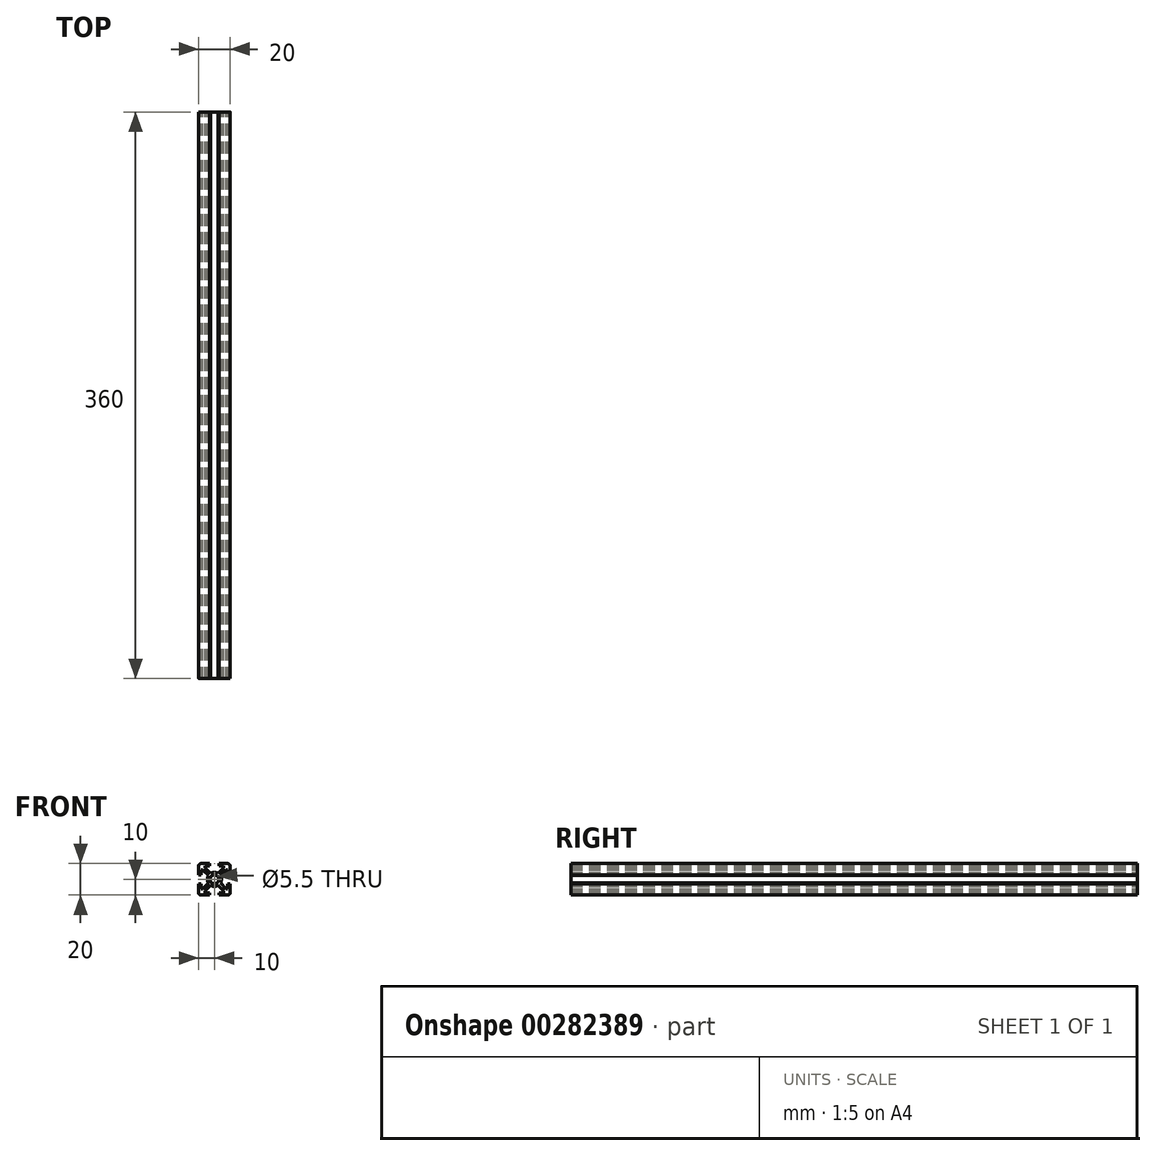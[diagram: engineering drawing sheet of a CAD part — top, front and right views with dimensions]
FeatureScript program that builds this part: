
annotation { "Feature Type Name" : "Feature", "Feature Type Description" : "" }
export const myFeature = defineFeature(function(context is Context, id is Id, definition is map)
    precondition{}
    {
        {
            var Q0;
            Q0=qCreatedBy(makeId("Front.planeOp"),FACE);
            var sketch = newSketch(context, id + "F0", { "sketchPlane" : qUnion([Q0])});
            skLineSegment(sketch, "E0.bottom", {"start": v(1.5, 0) * mm, "end": v(7, 0) * mm});
            skLineSegment(sketch, "E0.top", {"start": v(1.5, 20) * mm, "end": v(7, 20) * mm});
            skLineSegment(sketch, "E0.left", {"start": v(0, 1.5) * mm, "end": v(0, 7) * mm});
            skLineSegment(sketch, "E0.right", {"start": v(20, 1.5) * mm, "end": v(20, 7) * mm});
            skPoint(sketch, "E1.visualSharp", {"position": v(0, 20) * mm});
            skArc(sketch, "E1.filletArc", {"start": v(1.5, 20) * mm, "mid": v(0.44, 19.56) * mm, "end": v(0, 18.5) * mm});
            skPoint(sketch, "E2.visualSharp", {"position": v(20, 20) * mm});
            skArc(sketch, "E2.filletArc", {"start": v(20, 18.5) * mm, "mid": v(19.56, 19.56) * mm, "end": v(18.5, 20) * mm});
            skPoint(sketch, "E3.visualSharp", {"position": v(20, 0) * mm});
            skArc(sketch, "E3.filletArc", {"start": v(18.5, 0) * mm, "mid": v(19.56, 0.44) * mm, "end": v(20, 1.5) * mm});
            skPoint(sketch, "E4.visualSharp", {"position": v(0, 0) * mm});
            skArc(sketch, "E4.filletArc", {"start": v(0, 1.5) * mm, "mid": v(0.44, 0.44) * mm, "end": v(1.5, 0) * mm});
            skCircle(sketch, "E5", {"center": v(10, 10) * mm, "radius": 2.75 * mm});
            skPoint(sketch, "E5.centerSnap0", {"position": v(10, 0) * mm});
            skPoint(sketch, "E5.centerSnap1", {"position": v(0, 10) * mm});
            skArc(sketch, "E6", {"start": v(13.8, 7.6) * mm, "mid": v(14.5, 10) * mm, "end": v(13.8, 12.4) * mm});
            skLineSegment(sketch, "E7", {"start": v(10, 10) * mm, "end": v(18.5, 1.5) * mm, "construction": true});
            skLineSegment(sketch, "E8", {"start": v(10, 10) * mm, "end": v(18.5, 18.5) * mm, "construction": true});
            skLineSegment(sketch, "E9", {"start": v(10, 10) * mm, "end": v(20, 10) * mm, "construction": true});
            skLineSegment(sketch, "E10", {"start": v(10, 10) * mm, "end": v(10, 20) * mm, "construction": true});
            skLineSegment(sketch, "E11", {"start": v(10, 10) * mm, "end": v(1.5, 18.5) * mm, "construction": true});
            skLineSegment(sketch, "E12", {"start": v(10, 10) * mm, "end": v(0, 10) * mm, "construction": true});
            skLineSegment(sketch, "E13", {"start": v(10, 10) * mm, "end": v(1.5, 1.5) * mm, "construction": true});
            skLineSegment(sketch, "E14", {"start": v(10, 10) * mm, "end": v(10, 0) * mm, "construction": true});
            skLineSegment(sketch, "E15.trimOffspring", {"start": v(12.4, 6.2) * mm, "end": v(16, 2.59) * mm});
            skLineSegment(sketch, "E16.trimOffspring", {"start": v(13.8, 7.6) * mm, "end": v(17.41, 4) * mm});
            skLineSegment(sketch, "E17.trimOffspring", {"start": v(13.8, 12.4) * mm, "end": v(17.41, 16) * mm});
            skArc(sketch, "E18.trimOffspring", {"start": v(12.4, 13.8) * mm, "mid": v(10, 14.5) * mm, "end": v(7.6, 13.8) * mm});
            skLineSegment(sketch, "E19.trimOffspring", {"start": v(12.4, 13.8) * mm, "end": v(16, 17.41) * mm});
            skLineSegment(sketch, "E20.trimOffspring", {"start": v(7.6, 13.8) * mm, "end": v(4, 17.41) * mm});
            skArc(sketch, "E21.trimOffspring", {"start": v(6.2, 12.4) * mm, "mid": v(5.5, 10) * mm, "end": v(6.2, 7.6) * mm});
            skLineSegment(sketch, "E22.trimOffspring", {"start": v(6.2, 12.4) * mm, "end": v(2.59, 16) * mm});
            skLineSegment(sketch, "E23.trimOffspring", {"start": v(6.2, 7.6) * mm, "end": v(2.59, 4) * mm});
            skArc(sketch, "E24.trimOffspring", {"start": v(7.6, 6.2) * mm, "mid": v(10, 5.5) * mm, "end": v(12.4, 6.2) * mm});
            skLineSegment(sketch, "E25.trimOffspring", {"start": v(7.6, 6.2) * mm, "end": v(4, 2.59) * mm});
            skLineSegment(sketch, "E26", {"start": v(2.59, 16) * mm, "end": v(1.5, 16) * mm});
            skLineSegment(sketch, "E27", {"start": v(1.5, 16) * mm, "end": v(1.5, 13) * mm});
            skLineSegment(sketch, "E28", {"start": v(1.5, 13) * mm, "end": v(0, 13) * mm});
            skLineSegment(sketch, "E29", {"start": v(0, 7) * mm, "end": v(1.5, 7) * mm});
            skLineSegment(sketch, "E30", {"start": v(1.5, 7) * mm, "end": v(1.5, 4) * mm});
            skLineSegment(sketch, "E31", {"start": v(1.5, 4) * mm, "end": v(2.59, 4) * mm});
            skLineSegment(sketch, "E32", {"start": v(7, 20) * mm, "end": v(7, 18.5) * mm});
            skLineSegment(sketch, "E33", {"start": v(7, 18.5) * mm, "end": v(4, 18.5) * mm});
            skLineSegment(sketch, "E34", {"start": v(4, 18.5) * mm, "end": v(4, 17.41) * mm});
            skLineSegment(sketch, "E35", {"start": v(13, 20) * mm, "end": v(13, 18.5) * mm});
            skLineSegment(sketch, "E36", {"start": v(13, 18.5) * mm, "end": v(16, 18.5) * mm});
            skLineSegment(sketch, "E37", {"start": v(16, 18.5) * mm, "end": v(16, 17.41) * mm});
            skLineSegment(sketch, "E38", {"start": v(20, 13) * mm, "end": v(18.5, 13) * mm});
            skLineSegment(sketch, "E39", {"start": v(18.5, 13) * mm, "end": v(18.5, 16) * mm});
            skLineSegment(sketch, "E40", {"start": v(18.5, 16) * mm, "end": v(17.41, 16) * mm});
            skLineSegment(sketch, "E41", {"start": v(20, 7) * mm, "end": v(18.5, 7) * mm});
            skLineSegment(sketch, "E42", {"start": v(18.5, 7) * mm, "end": v(18.5, 4) * mm});
            skLineSegment(sketch, "E43", {"start": v(18.5, 4) * mm, "end": v(17.41, 4) * mm});
            skLineSegment(sketch, "E44", {"start": v(7, 0) * mm, "end": v(7, 1.5) * mm});
            skLineSegment(sketch, "E45", {"start": v(7, 1.5) * mm, "end": v(4, 1.5) * mm});
            skLineSegment(sketch, "E46", {"start": v(4, 1.5) * mm, "end": v(4, 2.59) * mm});
            skLineSegment(sketch, "E47", {"start": v(13, 0) * mm, "end": v(13, 1.5) * mm});
            skLineSegment(sketch, "E48", {"start": v(13, 1.5) * mm, "end": v(16, 1.5) * mm});
            skLineSegment(sketch, "E49", {"start": v(16, 1.5) * mm, "end": v(16, 2.59) * mm});
            skLineSegment(sketch, "E50.trimOffspring", {"start": v(13, 20) * mm, "end": v(18.5, 20) * mm});
            skLineSegment(sketch, "E51.trimOffspring", {"start": v(20, 13) * mm, "end": v(20, 18.5) * mm});
            skLineSegment(sketch, "E52.trimOffspring", {"start": v(13, 0) * mm, "end": v(18.5, 0) * mm});
            skLineSegment(sketch, "E53.trimOffspring", {"start": v(0, 13) * mm, "end": v(0, 18.5) * mm});
            skSolve(sketch);
        }
        {
            var Q0;
            Q0=qSketchRegion(id+"F0",true);
            extrude(context, id + "F1", {"entities" : qUnion([Q0]), "depth" : 360 * mm});
        }
    });
